# Revit family: PDT4P
name_source: partatom
category: Plumbing Fixtures
revit_build: Autodesk Revit 2015 (Build: 20140606_1530(x64)
units: mm (PartAtom-declared; Revit-internal decimal feet)

## types (7) — shared parameters
Aluminium = Aluminum - Polished
Chrome = Chrome - Polished
Glass = Glass
Manufacturer = SanSwiss
Model = PD4P
URL = http://www.sanswiss.com

## per-type parameters (varying)
| type | A | Polycarbonate |
| 800 | 800 mm  [stored 2.62467 ft] | <By Category> |
| 700 | 700 mm  [stored 2.29659 ft] | <By Category> |
| 750 | 750 mm  [stored 2.46063 ft] | <By Category> |
| 900 | 900 mm  [stored 2.95276 ft] | <By Category> |
| 1000 | 1000 mm  [stored 3.28084 ft] | Seal |
| 1200 | 1200 mm | <By Category> |
| 1400 | 1400 mm  [stored 4.59318 ft] | <By Category> |

note: [stored X ft] marks values corroborated as IEEE doubles in the binary element streams (Revit-internal decimal feet)

## geometry (parser evidence)
native form markers: Sweep x9
no freeform markers — native parametric forms only
